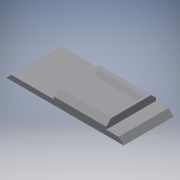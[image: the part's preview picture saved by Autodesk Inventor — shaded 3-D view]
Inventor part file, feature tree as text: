
AUTODESK INVENTOR PART (.ipt)
format: ipt  version: 2018.3 (Build 223284000, 284)  size: 293,888 bytes
history: native  units: mm
features: extrude x6, sketch x6, chamfer x4
ambient origin geometry x8: Origin, YZ Plane, XZ Plane, XY Plane, X Axis, Y Axis, Z Axis, Center Point
bodies: Solid1 (feature_tree)
feature tree (16):
  extrude  "Extrusion1"  Depth=20.0mm
  extrude  "Extrusion2"  Depth=2.0mm
  extrude  "Extrusion6"  Depth=20.0mm TaperAngle=0.0deg
  extrude  "Extrusion7"  Depth=20.0mm
  extrude  "Extrusion8"  Depth=3.75mm
  chamfer  "Chamfer7"  Distance=6.0mm
  chamfer  "Chamfer8"  Distance=3.0mm
  extrude  "Extrusion9"  Depth=2.0mm
  chamfer  "Chamfer9"  Angle=45.0deg  [1 undecoded]
  chamfer  "Chamfer10"  Distance=3.0mm
  sketch  "Sketch1"  dims[d0=43.0mm d1=20.0mm]
  sketch  "Sketch2"  dims[d2=2.0mm d3=0.0mm d4=2.0mm]
  sketch  "Sketch6"  dims[d5=2.0mm d6=20.0mm d7=0.0mm]
  sketch  "Sketch7"  dims[d47=20.0mm d48=12.5mm]
  sketch  "Sketch8"  dims[d49=3.75mm d50=3.75mm]
  sketch  "Sketch9"  dims[d51=6.0mm d52=6.0mm d53=3.0mm d54=0.0mm d55=2.12mm d56=45.0deg d57=3.0mm d58=0.0mm d59=2.12mm d60=45.0deg d61=3.0mm d62=0.0mm d63=2.0mm d64=2.0mm d65=45.0deg d66=2.0mm d67=2.0mm d68=45.0deg d69=1.0mm d70=3.0mm d71=0.0mm d72=2.0mm d73=2.0mm d74=45.0deg d75=2.0mm d76=2.0mm d77=45.0deg]
note: 1 required parameter value undecoded (feature->parameter linkage not recoverable at this tier; creation-order binding heuristic only, values carry confidence <= 0.55)
